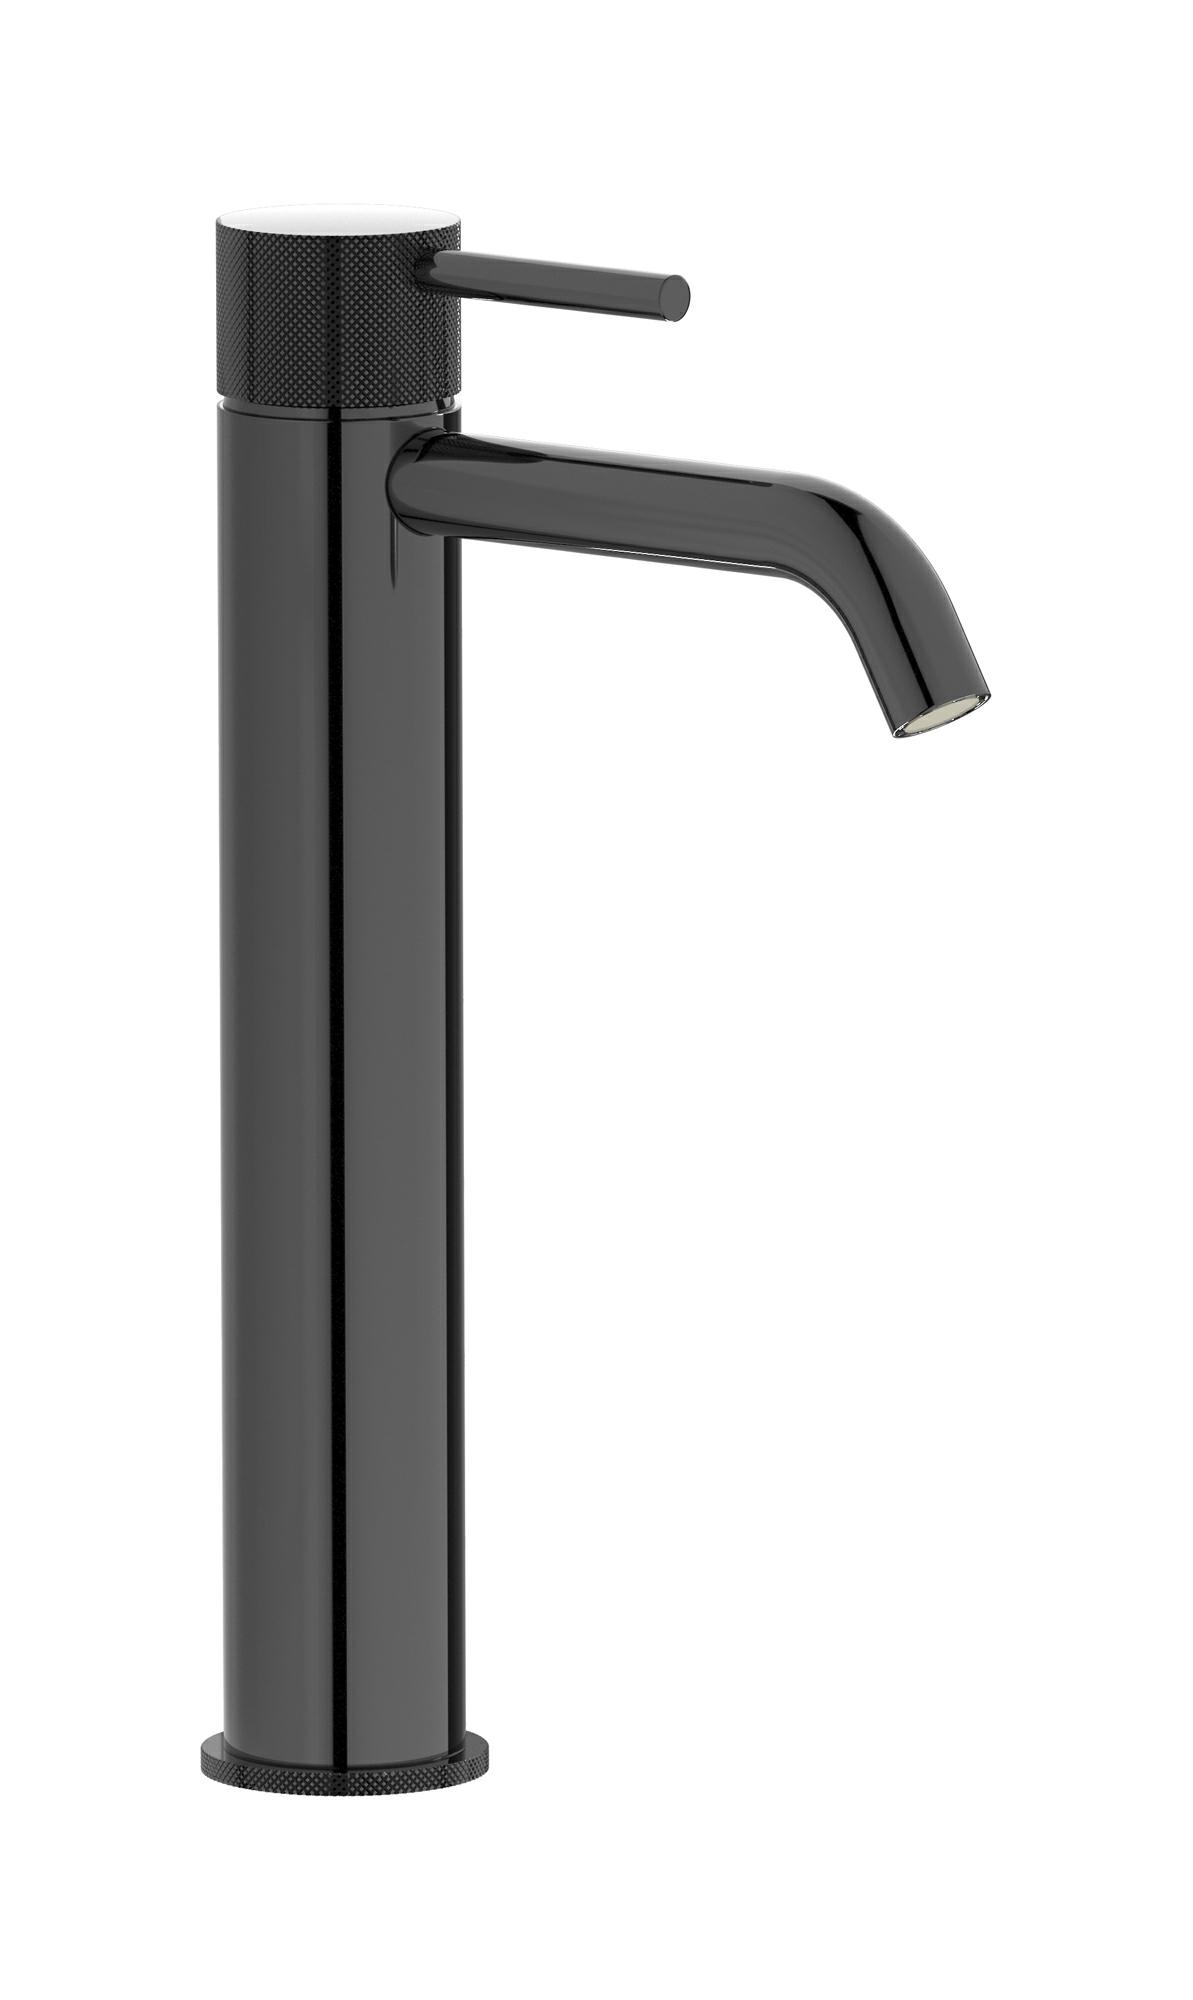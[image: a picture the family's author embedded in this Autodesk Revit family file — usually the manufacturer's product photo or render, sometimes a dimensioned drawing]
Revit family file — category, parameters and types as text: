
# Revit family: ID202
name_source: partatom
category: Apparecchi idraulici
units: mm (PartAtom-declared; Revit-internal decimal feet)

## family parameters
Basato su piano di lavoro = No
Condiviso = No
Mantieni orientamento annotazione = No
Numero OmniClass = 23.45.55.14
Punto di calcolo locali = No
Quota connettore circolare = Usa diametro
Sempre verticale = Sì
Taglio con vuoti quando caricato = No
Tipo di parte = Normale
Titolo OmniClass = Single Faucets

## types (12) — shared parameters
Cold water inlet = 10 mm  [stored 0.0328084 ft]
Commenti sul tipo = Washbasin mixer
Connessione CW = No
Connessione HW = No
Connessione di scarico = No
Connessione di ventilazione = No
Descrizione = Tall monohole washbasin mixer complete with drain
Hot water inlet = 10 mm  [stored 0.0328084 ft]
Produttore = IB Rubinetterie S.p.A.
URL = https://www.weareib.it
zero-valued in all types: Prospetto di default

## per-type parameters (varying)
| type | Finishes surface | Immagine tipo | Modello |
| Chrome | IB_Chrome | ID202CC.jpg | ID202CC |
| Brushed nickel | IB_Brushed nickel | ID202SS.jpg | ID202SS |
| Natural brass | IB_Brass | ID202ON.jpg | ID202ON |
| Matt black | IB_matt black | ID202NP.jpg | ID202NP |
| Black chrome | IB_Black chrome | ID202CF.jpg | ID202CF |
| Brushed black chrome | IB_Brushed black chrome | ID202CS.jpg | ID202CS |
| Pale gold | IB_Pale gold | ID202II.jpg | ID202II |
| Brushed pale gold | IB_brushed pale gold | ID202IS.jpg | ID202IS |
| Rose gold | IB_Rose gold | ID202RS.jpg | ID202RS |
| Brushed rose gold | IB_Brushed rose gold | ID202SR.jpg | ID202SR |
| Gold | IB_gold | ID202OO.jpg | ID202OO |
| Brushed gold | IB_brushed gold | ID202OS.jpg | ID202OS |

note: [stored X ft] marks values corroborated as IEEE doubles in the binary element streams (Revit-internal decimal feet)
